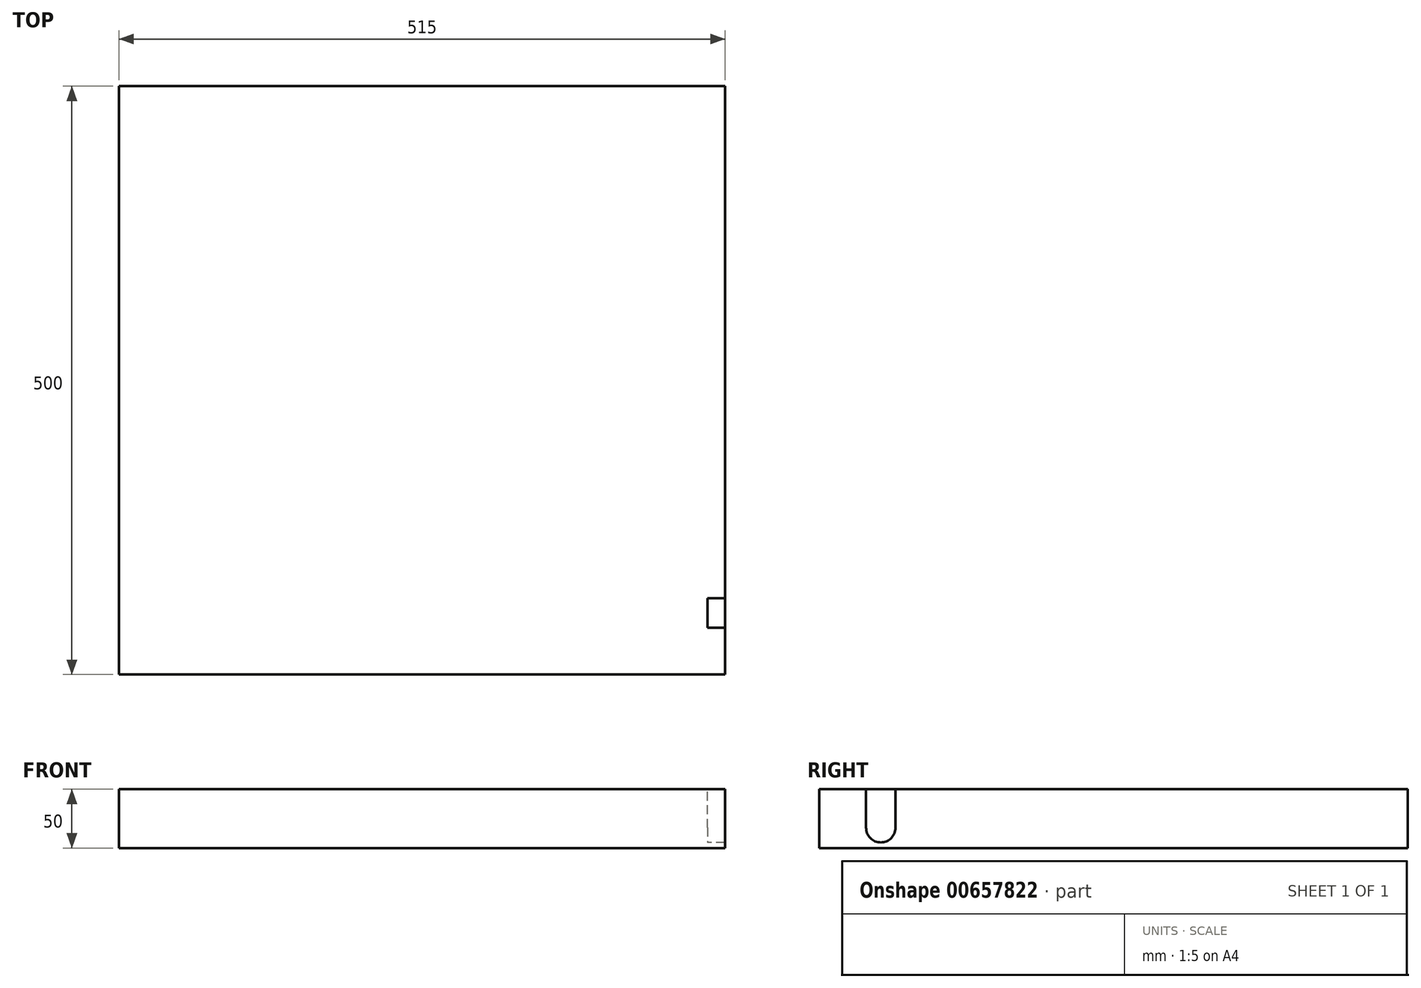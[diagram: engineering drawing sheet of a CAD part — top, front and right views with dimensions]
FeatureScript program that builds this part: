
annotation { "Feature Type Name" : "Feature", "Feature Type Description" : "" }
export const myFeature = defineFeature(function(context is Context, id is Id, definition is map)
    precondition{}
    {
        {
            var Q0;
            Q0=qCreatedBy(makeId("Top.planeOp"),FACE);
            var sketch = newSketch(context, id + "F0", { "sketchPlane" : qUnion([Q0])});
            skLineSegment(sketch, "E0.bottom", {"start": v(250, 250) * mm, "end": v(-250, 250) * mm});
            skLineSegment(sketch, "E0.top", {"start": v(250, -250) * mm, "end": v(-250, -250) * mm});
            skLineSegment(sketch, "E0.left", {"start": v(250, 250) * mm, "end": v(250, -250) * mm});
            skLineSegment(sketch, "E0.right", {"start": v(-250, 250) * mm, "end": v(-250, -250) * mm});
            skPoint(sketch, "E0.middle", {"position": v(0, 0) * mm});
            skSolve(sketch);
        }
        {
            var Q0;
            Q0=makeQuery(id+"F0.imprint","IMPRINT",FACE,{"disambiguationData":[TD([[makeQuery(id+"F0.imprint","IMPRINT",EDGE,{"derivedFrom":sQuery(id+"F0.wireOp",EDGE,"E0.bottom")}),1.0]])]});
            extrude(context, id + "F1", {"entities" : qUnion([Q0]), "depth" : 50 * mm, "offsetDistance" : 25 * mm});
        }
        {
            var Q0;
            Q0=makeQuery(id+"F1.opExtrude","SWEPT_FACE",FACE,{"disambiguationData":[OSD([sQuery(id+"F0.wireOp",EDGE,"E0.left")])]});
            var sketch = newSketch(context, id + "F2", { "sketchPlane" : qUnion([Q0])});
            skCircle(sketch, "E1", {"center": v(-197.68, 17.26) * mm, "radius": 12.5 * mm});
            skLineSegment(sketch, "E2.bottom", {"start": v(-185.18, 17.26) * mm, "end": v(-210.18, 17.26) * mm});
            skLineSegment(sketch, "E2.top", {"start": v(-185.18, 42.26) * mm, "end": v(-210.18, 42.26) * mm});
            skLineSegment(sketch, "E2.left", {"start": v(-185.18, 17.26) * mm, "end": v(-185.18, 42.26) * mm});
            skLineSegment(sketch, "E2.right", {"start": v(-210.18, 17.26) * mm, "end": v(-210.18, 42.26) * mm});
            skPoint(sketch, "E2.middle", {"position": v(-197.68, 29.76) * mm});
            skLineSegment(sketch, "E3.bottom", {"start": v(-210.18, 42.26) * mm, "end": v(-185.18, 42.26) * mm});
            skLineSegment(sketch, "E3.top", {"start": v(-210.18, 50) * mm, "end": v(-185.18, 50) * mm});
            skLineSegment(sketch, "E3.left", {"start": v(-210.18, 42.26) * mm, "end": v(-210.18, 50) * mm});
            skLineSegment(sketch, "E3.right", {"start": v(-185.18, 42.26) * mm, "end": v(-185.18, 50) * mm});
            skSolve(sketch);
        }
        {
            var Q0;
            {var subQ2=sQuery(id+"F2.wireOp",EDGE,"E2.left");Q0=makeQuery(id+"F2.imprint","IMPRINT",FACE,{"disambiguationData":[TD([[makeQuery(id+"F2.imprint","IMPRINT",EDGE,{"derivedFrom":subQ2}),-1.0]])]});}
            extrude(context, id + "F3", {"entities" : qUnion([Q0]), "operationType" : NewBodyOperationType.ADD, "depth" : 15 * mm, "offsetDistance" : 25 * mm});
        }
    });
